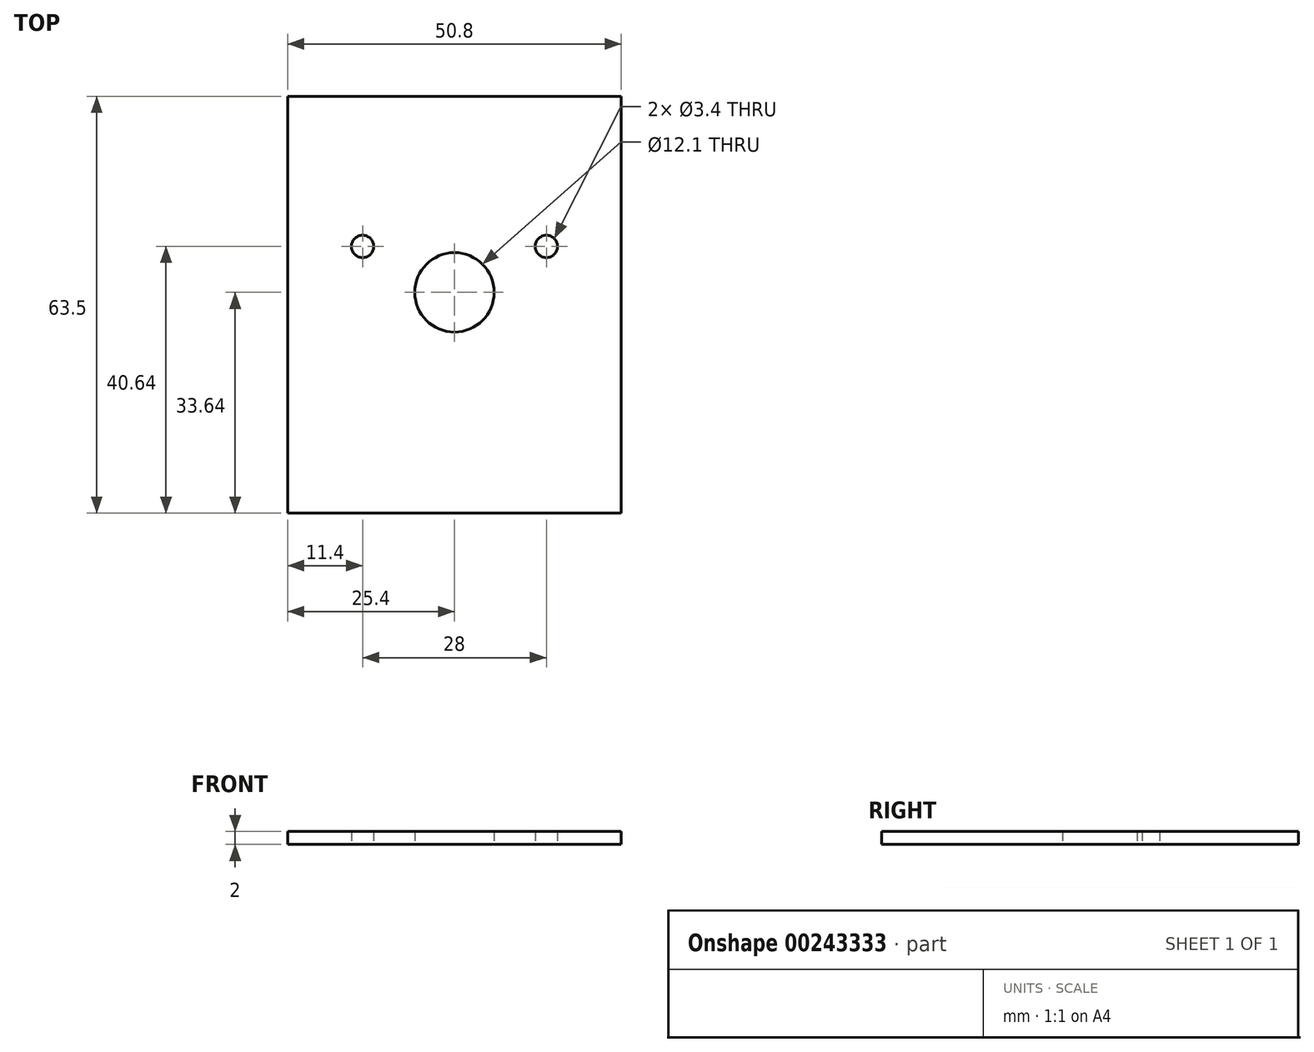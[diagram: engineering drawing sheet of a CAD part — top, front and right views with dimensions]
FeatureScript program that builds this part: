
annotation { "Feature Type Name" : "Feature", "Feature Type Description" : "" }
export const myFeature = defineFeature(function(context is Context, id is Id, definition is map)
    precondition{}
    {
        {
            var Q0;
            Q0=qCreatedBy(makeId("Top.planeOp"),FACE);
            var sketch = newSketch(context, id + "F0", { "sketchPlane" : qUnion([Q0])});
            skLineSegment(sketch, "E0.bottom", {"start": v(-25.4, 31.75) * mm, "end": v(25.4, 31.75) * mm});
            skLineSegment(sketch, "E0.top", {"start": v(-25.4, -31.75) * mm, "end": v(25.4, -31.75) * mm});
            skLineSegment(sketch, "E0.left", {"start": v(-25.4, 31.75) * mm, "end": v(-25.4, -31.75) * mm});
            skLineSegment(sketch, "E0.right", {"start": v(25.4, 31.75) * mm, "end": v(25.4, -31.75) * mm});
            skPoint(sketch, "E0.middle", {"position": v(0, 0) * mm});
            skCircle(sketch, "E1", {"center": v(0, 8.89) * mm, "radius": 18.5 * mm, "construction": true});
            skLineSegment(sketch, "E2", {"start": v(-18.5, 8.89) * mm, "end": v(18.5, 8.89) * mm, "construction": true});
            skCircle(sketch, "E3", {"center": v(-14, 8.89) * mm, "radius": 1.7 * mm});
            skLineSegment(sketch, "E4", {"start": v(0, 27.39) * mm, "end": v(0, -9.61) * mm, "construction": true});
            skCircle(sketch, "E5.MirrorC", {"center": v(14, 8.9) * mm, "radius": 1.7 * mm});
            skLineSegment(sketch, "E6.bottom", {"start": v(-25.4, -31.75) * mm, "end": v(25.4, -31.75) * mm, "construction": true});
            skLineSegment(sketch, "E6.top", {"start": v(-25.4, -15.75) * mm, "end": v(25.4, -15.75) * mm, "construction": true});
            skLineSegment(sketch, "E6.left", {"start": v(-25.4, -31.75) * mm, "end": v(-25.4, -15.75) * mm, "construction": true});
            skLineSegment(sketch, "E6.right", {"start": v(25.4, -31.75) * mm, "end": v(25.4, -15.75) * mm, "construction": true});
            skCircle(sketch, "E7", {"center": v(0, 1.89) * mm, "radius": 6.05 * mm});
            skSolve(sketch);
        }
        {
            var Q0;
            Q0 = qSketchRegion(id + "F0", true);
            extrude(context, id + "F1", {"entities" : qUnion([Q0]), "depth" : 2 * mm});
        }
    });
